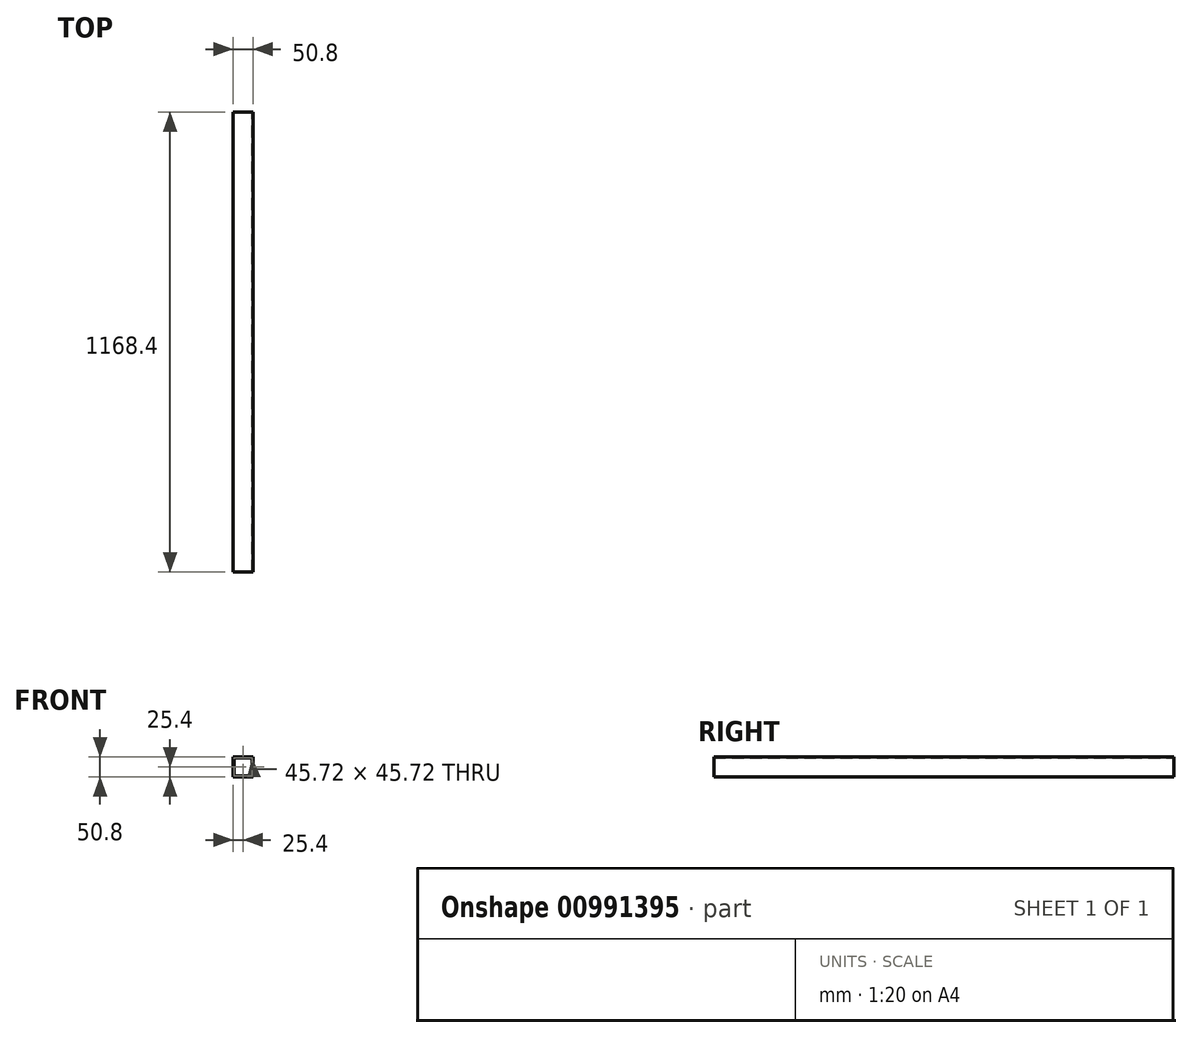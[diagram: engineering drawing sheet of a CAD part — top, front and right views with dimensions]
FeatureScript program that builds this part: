
annotation { "Feature Type Name" : "Feature", "Feature Type Description" : "" }
export const myFeature = defineFeature(function(context is Context, id is Id, definition is map)
    precondition{}
    {
        {
            var Q0;
            Q0=qCreatedBy(makeId("Front.planeOp"),FACE);
            var sketch = newSketch(context, id + "F0", { "sketchPlane" : qUnion([Q0])});
            skLineSegment(sketch, "E0.bottom", {"start": v(25.4, 25.4) * mm, "end": v(-25.4, 25.4) * mm});
            skLineSegment(sketch, "E0.top", {"start": v(25.4, -25.4) * mm, "end": v(-25.4, -25.4) * mm});
            skLineSegment(sketch, "E0.left", {"start": v(25.4, 25.4) * mm, "end": v(25.4, -25.4) * mm});
            skLineSegment(sketch, "E0.right", {"start": v(-25.4, 25.4) * mm, "end": v(-25.4, -25.4) * mm});
            skPoint(sketch, "E0.middle", {"position": v(0, 0) * mm});
            skLineSegment(sketch, "E1.0", {"start": v(-22.86, 22.86) * mm, "end": v(-22.86, -22.86) * mm});
            skLineSegment(sketch, "E1.1", {"start": v(22.86, 22.86) * mm, "end": v(-22.86, 22.86) * mm});
            skLineSegment(sketch, "E1.2", {"start": v(22.86, 22.86) * mm, "end": v(22.86, -22.86) * mm});
            skLineSegment(sketch, "E1.3", {"start": v(22.86, -22.86) * mm, "end": v(-22.86, -22.86) * mm});
            skSolve(sketch);
        }
        {
            var Q0;
            Q0=qSketchRegion(id+"F0",true);
            extrude(context, id + "F1", {"entities" : qUnion([Q0]), "endBound" : BoundingType.SYMMETRIC, "depth" : 1168.4 * mm, "offsetDistance" : 25.4 * mm});
        }
    });
